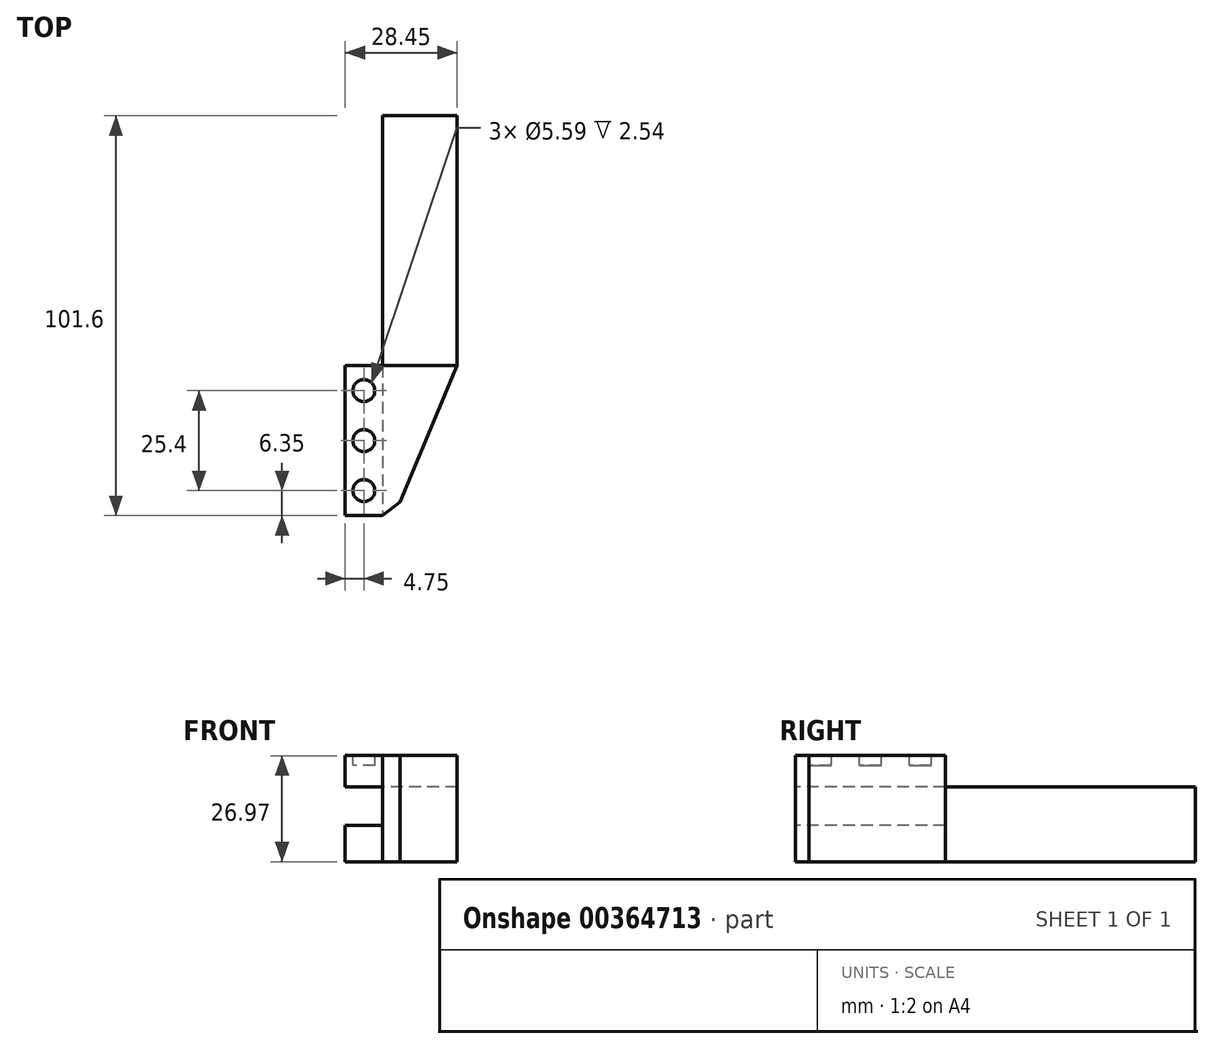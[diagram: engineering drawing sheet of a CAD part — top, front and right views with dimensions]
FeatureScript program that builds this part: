
annotation { "Feature Type Name" : "Feature", "Feature Type Description" : "" }
export const myFeature = defineFeature(function(context is Context, id is Id, definition is map)
    precondition{}
    {
        {
            var Q0;
            Q0=qCreatedBy(makeId("Top.planeOp"),FACE);
            var sketch = newSketch(context, id + "F0", { "sketchPlane" : qUnion([Q0])});
            skLineSegment(sketch, "E0", {"start": v(0, 0) * mm, "end": v(9.53, 0) * mm});
            skLineSegment(sketch, "E1", {"start": v(9.52, 0) * mm, "end": v(13.95, 3.42) * mm});
            skLineSegment(sketch, "E2", {"start": v(0, 0) * mm, "end": v(0, 38.1) * mm});
            skLineSegment(sketch, "E3", {"start": v(28.45, 38.1) * mm, "end": v(13.95, 3.42) * mm});
            skLineSegment(sketch, "E4", {"start": v(28.45, 38.1) * mm, "end": v(0, 38.1) * mm});
            skSolve(sketch);
        }
        {
            var Q0;
            Q0 = qSketchRegion(id + "F0", true);
            extrude(context, id + "F1", {"entities" : qUnion([Q0]), "depth" : 26.97 * mm});
        }
        {
            var Q0;
            Q0=makeQuery(id+"F1.opExtrude","SWEPT_FACE",FACE,{"disambiguationData":[OSD([sQuery(id+"F0.wireOp",EDGE,"E2")])]});
            var sketch = newSketch(context, id + "F2", { "sketchPlane" : qUnion([Q0])});
            skLineSegment(sketch, "E5.bottom", {"start": v(-38.1, 9.27) * mm, "end": v(0, 9.27) * mm});
            skLineSegment(sketch, "E5.top", {"start": v(-38.1, 19.05) * mm, "end": v(0, 19.05) * mm});
            skLineSegment(sketch, "E5.left", {"start": v(-38.1, 9.27) * mm, "end": v(-38.1, 19.05) * mm});
            skLineSegment(sketch, "E5.right", {"start": v(0, 9.27) * mm, "end": v(0, 19.05) * mm});
            skSolve(sketch);
        }
        {
            var Q0;
            Q0 = qSketchRegion(id + "F2", true);
            extrude(context, id + "F3", {"entities" : qUnion([Q0]), "operationType" : NewBodyOperationType.REMOVE, "oppositeDirection" : true, "depth" : 9.52 * mm});
        }
        {
            var Q0;
            Q0=makeQuery(id+"F1.opExtrude","SWEPT_FACE",FACE,{"disambiguationData":[OSD([sQuery(id+"F0.wireOp",EDGE,"E4")])]});
            var sketch = newSketch(context, id + "F4", { "sketchPlane" : qUnion([Q0])});
            skLineSegment(sketch, "E6.bottom", {"start": v(-28.45, 0) * mm, "end": v(-9.53, 0) * mm});
            skLineSegment(sketch, "E6.top", {"start": v(-28.45, 19.05) * mm, "end": v(-9.53, 19.05) * mm});
            skLineSegment(sketch, "E6.left", {"start": v(-28.45, 0) * mm, "end": v(-28.45, 19.05) * mm});
            skLineSegment(sketch, "E6.right", {"start": v(-9.53, 0) * mm, "end": v(-9.53, 19.05) * mm});
            skSolve(sketch);
        }
        {
            var Q0;
            Q0 = qSketchRegion(id + "F4", true);
            extrude(context, id + "F5", {"entities" : qUnion([Q0]), "operationType" : NewBodyOperationType.ADD, "depth" : 63.5 * mm});
        }
        {
            var Q0;
            Q0=makeQuery(id+"F1.opExtrude","CAP_FACE",FACE,{"disambiguationData":[OSD([sQuery(id+"F0.wireOp",EDGE,"E0"),sQuery(id+"F0.wireOp",EDGE,"E1"),sQuery(id+"F0.wireOp",EDGE,"E2"),sQuery(id+"F0.wireOp",EDGE,"E3"),sQuery(id+"F0.wireOp",EDGE,"E4")])],"isStart":false});
            var sketch = newSketch(context, id + "F6", { "sketchPlane" : qUnion([Q0])});
            skCircle(sketch, "E7", {"center": v(4.75, 31.75) * mm, "radius": 2.8 * mm});
            skCircle(sketch, "E8", {"center": v(4.75, 19.05) * mm, "radius": 2.8 * mm});
            skCircle(sketch, "E9", {"center": v(4.75, 6.35) * mm, "radius": 2.8 * mm});
            skSolve(sketch);
        }
        {
            var Q0;
            Q0 = qSketchRegion(id + "F6", true);
            extrude(context, id + "F7", {"entities" : qUnion([Q0]), "operationType" : NewBodyOperationType.REMOVE, "oppositeDirection" : true, "depth" : 2.54 * mm});
        }
    });
